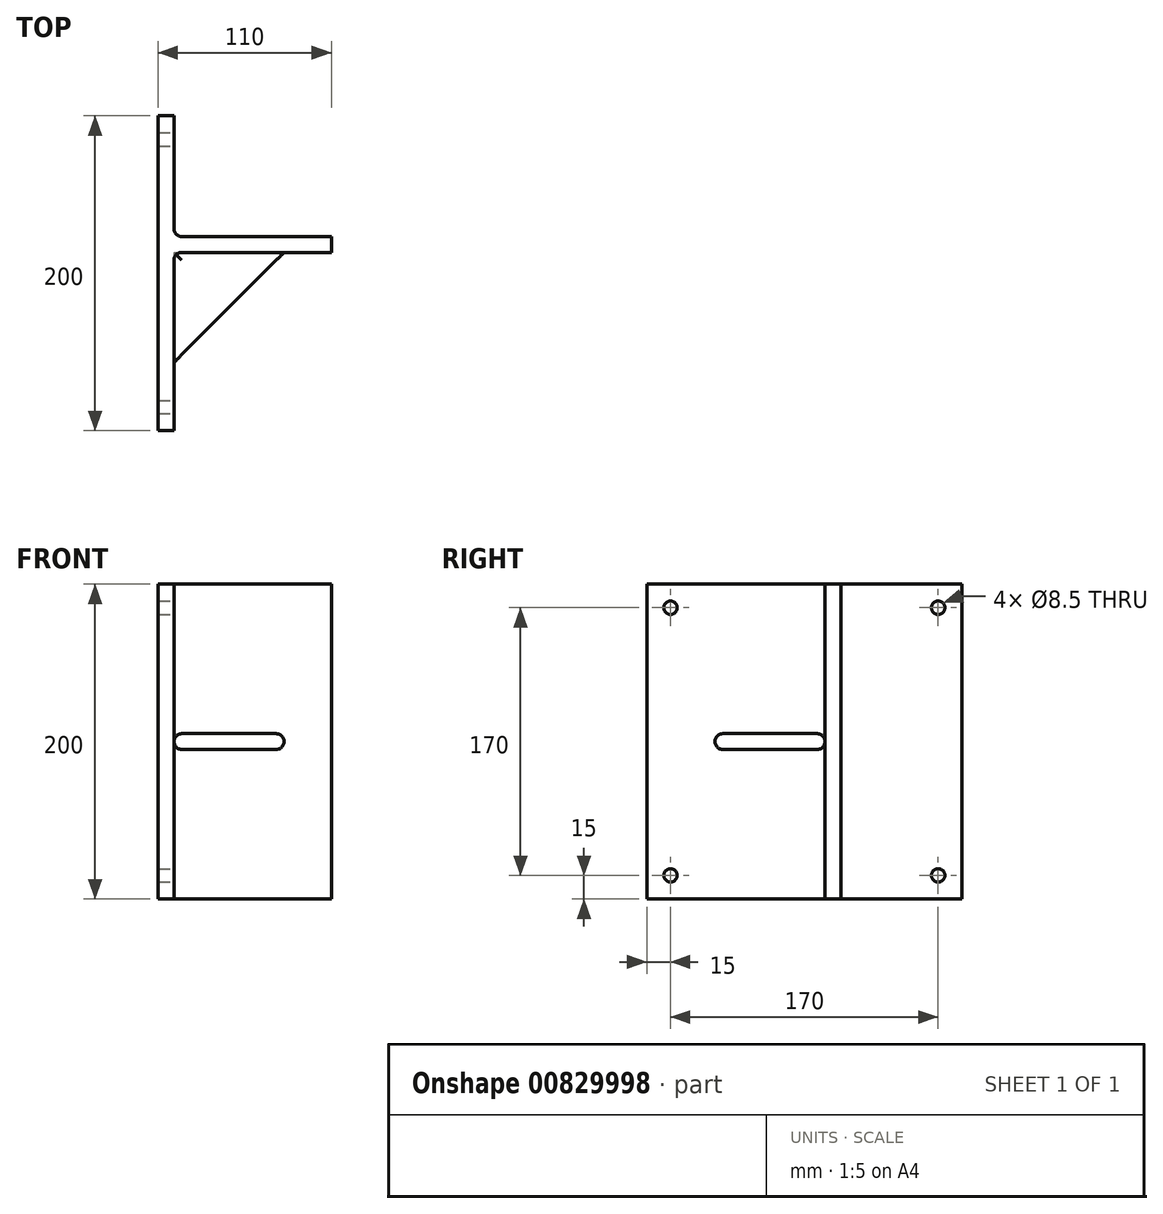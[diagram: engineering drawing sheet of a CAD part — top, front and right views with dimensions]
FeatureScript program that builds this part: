
annotation { "Feature Type Name" : "Feature", "Feature Type Description" : "" }
export const myFeature = defineFeature(function(context is Context, id is Id, definition is map)
    precondition{}
    {
        {
            var Q0;
            Q0=qCreatedBy(makeId("Top.planeOp"),FACE);
            var sketch = newSketch(context, id + "F0", { "sketchPlane" : qUnion([Q0])});
            skLineSegment(sketch, "E0.bottom", {"start": v(-5, 100) * mm, "end": v(5, 100) * mm});
            skLineSegment(sketch, "E0.top", {"start": v(-5, -100) * mm, "end": v(5, -100) * mm});
            skLineSegment(sketch, "E0.left", {"start": v(-5, 100) * mm, "end": v(-5, -100) * mm});
            skLineSegment(sketch, "E0.right", {"start": v(5, 100) * mm, "end": v(5, -100) * mm});
            skPoint(sketch, "E0.middle", {"position": v(0, 0) * mm});
            skLineSegment(sketch, "E1.bottom", {"start": v(5, 23.2) * mm, "end": v(105, 23.2) * mm});
            skLineSegment(sketch, "E1.top", {"start": v(5, 13.2) * mm, "end": v(105, 13.2) * mm});
            skLineSegment(sketch, "E1.left", {"start": v(5, 23.2) * mm, "end": v(5, 13.2) * mm});
            skLineSegment(sketch, "E1.right", {"start": v(105, 23.2) * mm, "end": v(105, 13.2) * mm});
            skSolve(sketch);
        }
        {
            var Q0;
            Q0 = qSketchRegion(id + "F0", true);
            extrude(context, id + "F1", {"entities" : qUnion([Q0]), "depth" : 200 * mm, "offsetDistance" : 25 * mm});
        }
        {
            var Q0;
            {var subQ0=sQuery(id+"F0.wireOp",EDGE,"E0.right");Q0=makeQuery(id+"F1.opExtrude","SWEPT_FACE",FACE,{"disambiguationData":[OSD([subQ0]),TDD([makeQuery(id+"F0.imprint","IMPRINT",EDGE,{"disambiguationData":[TD([[makeQuery(id+"F0.imprint","INTERSECT",VERTEX,{"derivedFrom":[sQuery(id+"F0.wireOp",EDGE,"E0.top"),subQ0]}),1.0]])],"derivedFrom":subQ0})])]});}
            var sketch = newSketch(context, id + "F2", { "sketchPlane" : qUnion([Q0])});
            skLineSegment(sketch, "E2.bottom", {"start": v(13.2, 105) * mm, "end": v(-56.8, 105) * mm});
            skLineSegment(sketch, "E2.top", {"start": v(13.2, 95) * mm, "end": v(-56.8, 95) * mm});
            skLineSegment(sketch, "E2.left", {"start": v(13.2, 105) * mm, "end": v(13.2, 95) * mm});
            skLineSegment(sketch, "E2.right", {"start": v(-56.8, 105) * mm, "end": v(-56.8, 95) * mm});
            skSolve(sketch);
        }
        {
            var Q0;
            Q0=makeQuery(id+"F2.imprint","IMPRINT",FACE,{"disambiguationData":[TD([[makeQuery(id+"F2.imprint","IMPRINT",EDGE,{"derivedFrom":sQuery(id+"F2.wireOp",EDGE,"E2.bottom")}),1.0]])]});
            extrude(context, id + "F3", {"entities" : qUnion([Q0]), "depth" : 70 * mm, "offsetDistance" : 25 * mm});
        }
        {
            var Q0;
            Q0=makeQuery(id+"F3.opExtrude","SWEPT_FACE",FACE,{"disambiguationData":[OSD([sQuery(id+"F2.wireOp",EDGE,"E2.bottom")])]});
            var sketch = newSketch(context, id + "F4", { "sketchPlane" : qUnion([Q0])});
            skLineSegment(sketch, "E3", {"start": v(5, -56.8) * mm, "end": v(75, 13.2) * mm});
            skSolve(sketch);
        }
        {
            var Q0;
            Q0 = qSketchRegion(id + "F4", true);
            var Q1;
            Q1=makeQuery(id+"F4.imprint","IMPRINT",FACE,{"disambiguationData":[TD([[makeQuery(id+"F4.imprint","IMPRINT",EDGE,{"derivedFrom":sQuery(id+"F4.wireOp",EDGE,"E3")}),-1.0]])]});
            extrude(context, id + "F5", {"entities" : qUnion([Q0, Q1]), "operationType" : NewBodyOperationType.REMOVE, "oppositeDirection" : true, "depth" : 70 * mm, "offsetDistance" : 25 * mm});
        }
        {
            var Q0;
            Q0=qCreatedBy(makeId("Right.planeOp"),FACE);
            var sketch = newSketch(context, id + "F6", { "sketchPlane" : qUnion([Q0])});
            skCircle(sketch, "E4", {"center": v(85, 185) * mm, "radius": 4.25 * mm});
            skCircle(sketch, "E5", {"center": v(85, 15) * mm, "radius": 4.25 * mm});
            skCircle(sketch, "E6", {"center": v(-85, 15) * mm, "radius": 4.25 * mm});
            skCircle(sketch, "E7", {"center": v(-85, 185) * mm, "radius": 4.25 * mm});
            skSolve(sketch);
        }
        {
            var Q0;
            Q0 = qSketchRegion(id + "F6", true);
            extrude(context, id + "F7", {"entities" : qUnion([Q0]), "operationType" : NewBodyOperationType.REMOVE, "endBound" : BoundingType.SYMMETRIC, "oppositeDirection" : true, "depth" : 25 * mm, "offsetDistance" : 25 * mm});
        }
        {
            var Q0;
            Q0=makeQuery(id+"F3.opExtrude","SWEPT_BODY",BODY,{"disambiguationData":[OSD([sQuery(id+"F2.wireOp",EDGE,"E2.bottom"),sQuery(id+"F2.wireOp",EDGE,"E2.top"),sQuery(id+"F2.wireOp",EDGE,"E2.left"),sQuery(id+"F2.wireOp",EDGE,"E2.right")])]});
            deleteBodies(context, id + "F8", {"entities" : qUnion([Q0])});
        }
        {
            var Q0;
            {var subQ0=sQuery(id+"F0.wireOp",EDGE,"E0.right");Q0=makeQuery(id+"F1.opExtrude","SWEPT_FACE",FACE,{"disambiguationData":[OSD([subQ0]),TDD([makeQuery(id+"F0.imprint","IMPRINT",EDGE,{"disambiguationData":[TD([[makeQuery(id+"F0.imprint","INTERSECT",VERTEX,{"derivedFrom":[sQuery(id+"F0.wireOp",EDGE,"E0.top"),subQ0]}),1.0]])],"derivedFrom":subQ0})])]});}
            var sketch = newSketch(context, id + "F9", { "sketchPlane" : qUnion([Q0])});
            skLineSegment(sketch, "E8.bottom", {"start": v(13.2, 105) * mm, "end": v(-56.8, 105) * mm});
            skLineSegment(sketch, "E8.top", {"start": v(13.2, 95) * mm, "end": v(-56.8, 95) * mm});
            skLineSegment(sketch, "E8.left", {"start": v(13.2, 105) * mm, "end": v(13.2, 95) * mm});
            skLineSegment(sketch, "E8.right", {"start": v(-56.8, 105) * mm, "end": v(-56.8, 95) * mm});
            skSolve(sketch);
        }
        {
            var Q0;
            Q0=makeQuery(id+"F9.imprint","IMPRINT",FACE,{"disambiguationData":[TD([[makeQuery(id+"F9.imprint","IMPRINT",EDGE,{"derivedFrom":sQuery(id+"F9.wireOp",EDGE,"E8.bottom")}),1.0]])]});
            extrude(context, id + "F10", {"entities" : qUnion([Q0]), "depth" : 70 * mm, "offsetDistance" : 25 * mm});
        }
        {
            var Q0;
            Q0=makeQuery(id+"F10.opExtrude","SWEPT_FACE",FACE,{"disambiguationData":[OSD([sQuery(id+"F9.wireOp",EDGE,"E8.bottom")])]});
            var sketch = newSketch(context, id + "F11", { "sketchPlane" : qUnion([Q0])});
            skLineSegment(sketch, "E9", {"start": v(5, -56.8) * mm, "end": v(75, 13.2) * mm});
            skSolve(sketch);
        }
        {
            var Q0;
            Q0=makeQuery(id+"F11.imprint","IMPRINT",FACE,{"disambiguationData":[TD([[makeQuery(id+"F11.imprint","IMPRINT",EDGE,{"derivedFrom":sQuery(id+"F11.wireOp",EDGE,"E9")}),-1.0]])]});
            extrude(context, id + "F12", {"entities" : qUnion([Q0]), "operationType" : NewBodyOperationType.REMOVE, "oppositeDirection" : true, "depth" : 25 * mm, "offsetDistance" : 25 * mm});
        }
        {
            var Q0;
            Q0=makeQuery(id+"F1.opExtrude","SWEPT_EDGE",EDGE,{"disambiguationData":[OSD([sQuery(id+"F0.wireOp",EDGE,"E0.right"),sQuery(id+"F0.wireOp",EDGE,"E1.top"),sQuery(id+"F0.wireOp",EDGE,"E1.left")])]});
            var Q1;
            Q1=makeQuery(id+"F10.opExtrude","SWEPT_EDGE",EDGE,{"disambiguationData":[OSD([sQuery(id+"F0.wireOp",EDGE,"E0.right"),sQuery(id+"F0.wireOp",EDGE,"E1.top"),sQuery(id+"F0.wireOp",EDGE,"E1.left"),sQuery(id+"F9.wireOp",EDGE,"E8.bottom"),sQuery(id+"F9.wireOp",EDGE,"E8.left")])]});
            var Q2;
            Q2=makeQuery(id+"F10.opExtrude","CAP_EDGE",EDGE,{"disambiguationData":[OSD([sQuery(id+"F9.wireOp",EDGE,"E8.bottom")])],"isStart":true});
            var Q3;
            Q3=makeQuery(id+"F10.opExtrude","CAP_EDGE",EDGE,{"disambiguationData":[OSD([sQuery(id+"F9.wireOp",EDGE,"E8.top")])],"isStart":true});
            var Q4;
            Q4=makeQuery(id+"F10.opExtrude","SWEPT_EDGE",EDGE,{"disambiguationData":[OSD([sQuery(id+"F0.wireOp",EDGE,"E0.right"),sQuery(id+"F0.wireOp",EDGE,"E1.top"),sQuery(id+"F0.wireOp",EDGE,"E1.left"),sQuery(id+"F9.wireOp",EDGE,"E8.top"),sQuery(id+"F9.wireOp",EDGE,"E8.left")])]});
            var Q5;
            Q5=makeQuery(id+"F1.opExtrude","SWEPT_EDGE",EDGE,{"disambiguationData":[OSD([sQuery(id+"F0.wireOp",EDGE,"E0.right"),sQuery(id+"F0.wireOp",EDGE,"E1.bottom"),sQuery(id+"F0.wireOp",EDGE,"E1.left")])]});
            fillet(context, id + "F13", {"entities" : qUnion([Q0, Q1, Q2, Q3, Q4, Q5]), "radius" : 5 * mm, "tangentPropagation" : true, "allowEdgeOverflow" : false});
        }
    });
